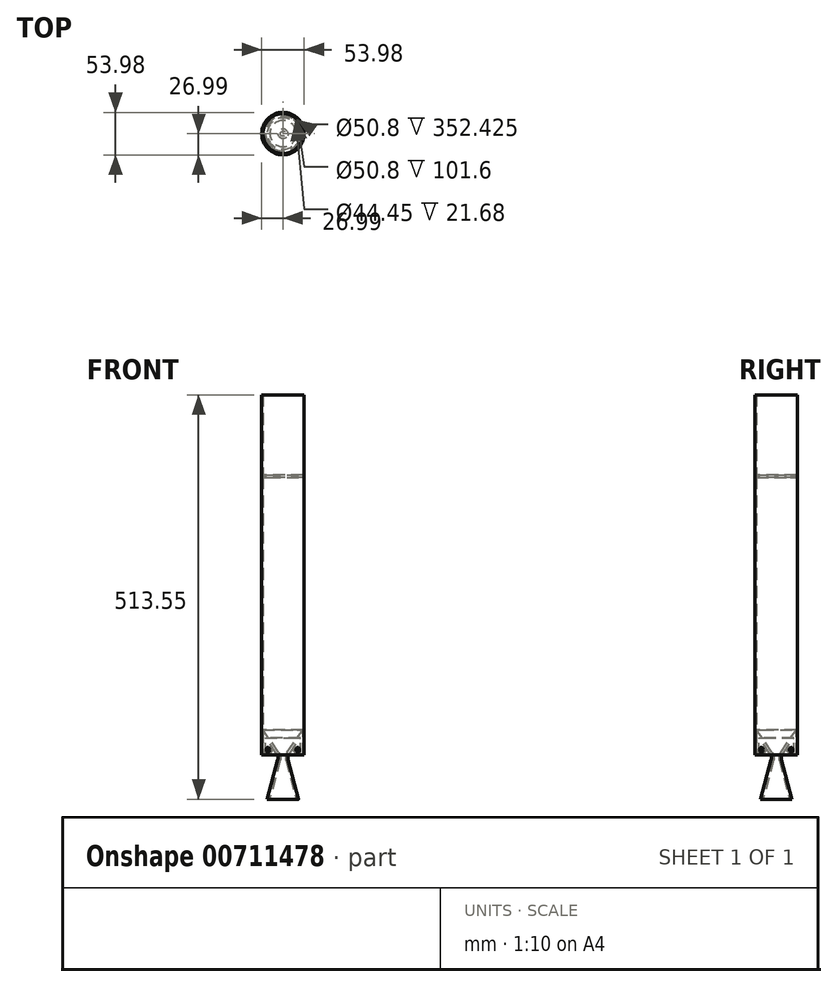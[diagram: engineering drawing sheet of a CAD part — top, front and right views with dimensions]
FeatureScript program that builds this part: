
annotation { "Feature Type Name" : "Feature", "Feature Type Description" : "" }
export const myFeature = defineFeature(function(context is Context, id is Id, definition is map)
    precondition{}
    {
        {
            var Q0;
            Q0=qCreatedBy(makeId("Front.planeOp"),FACE);
            var sketch = newSketch(context, id + "F0", { "sketchPlane" : qUnion([Q0])});
            skLineSegment(sketch, "E0", {"start": v(0, 0) * mm, "end": v(-25.4, 0) * mm, "construction": true});
            skLineSegment(sketch, "E1", {"start": v(-25.4, 0) * mm, "end": v(-5.47, -28.46) * mm});
            skArc(sketch, "E2", {"start": v(-5.47, -28.46) * mm, "mid": v(-3.37, -33.54) * mm, "end": v(-3.6, -39.03) * mm});
            skLineSegment(sketch, "E3", {"start": v(-3.18, -35.74) * mm, "end": v(0, -35.74) * mm, "construction": true});
            skLineSegment(sketch, "E4", {"start": v(-3.6, -39.03) * mm, "end": v(-16.76, -88.1) * mm});
            skLineSegment(sketch, "E5", {"start": v(-25.4, 0) * mm, "end": v(-25.4, -31.75) * mm});
            skLineSegment(sketch, "E6", {"start": v(-25.4, -31.75) * mm, "end": v(-22.22, -31.75) * mm});
            skLineSegment(sketch, "E7", {"start": v(-22.23, -10.07) * mm, "end": v(-8.07, -30.28) * mm});
            skLineSegment(sketch, "E8", {"start": v(-5.47, -28.46) * mm, "end": v(-8.07, -30.28) * mm, "construction": true});
            skLineSegment(sketch, "E9", {"start": v(-22.22, -31.75) * mm, "end": v(-22.22, -10.07) * mm});
            skLineSegment(sketch, "E10", {"start": v(-3.6, -39.03) * mm, "end": v(-6.67, -38.21) * mm, "construction": true});
            skArc(sketch, "E11", {"start": v(-6.67, -38.21) * mm, "mid": v(-6.5, -34.1) * mm, "end": v(-8.07, -30.28) * mm});
            skLineSegment(sketch, "E12", {"start": v(0, 0) * mm, "end": v(0, -88.1) * mm, "construction": true});
            skLineSegment(sketch, "E13", {"start": v(0, -88.1) * mm, "end": v(-16.76, -88.1) * mm, "construction": true});
            skLineSegment(sketch, "E14", {"start": v(-6.67, -38.21) * mm, "end": v(-20.04, -88.1) * mm});
            skLineSegment(sketch, "E15", {"start": v(-20.04, -88.1) * mm, "end": v(-16.76, -88.1) * mm});
            skSolve(sketch);
        }
        {
            var Q0;
            Q0=makeQuery(id+"F0.imprint","IMPRINT",FACE,{"disambiguationData":[TD([[makeQuery(id+"F0.imprint","IMPRINT",EDGE,{"derivedFrom":sQuery(id+"F0.wireOp",EDGE,"E1")}),-1.0]])]});
            var Q1;
            Q1=sQuery(id+"F0.wireOp",EDGE,"E12");
            revolve(context, id + "F1", {"surfaceOperationType" : NewSurfaceOperationType.NEW, "entities" : qUnion([Q0]), "axis" : qUnion([Q1]), "revolveType" : RevolveType.FULL});
        }
        {
            var Q0;
            Q0=qCreatedBy(makeId("Front.planeOp"),FACE);
            var sketch = newSketch(context, id + "F2", { "sketchPlane" : qUnion([Q0])});
            skLineSegment(sketch, "E16", {"start": v(0, 0) * mm, "end": v(0, 457.2) * mm, "construction": true});
            skLineSegment(sketch, "E17", {"start": v(0, 457.2) * mm, "end": v(25.4, 457.2) * mm, "construction": true});
            skLineSegment(sketch, "E18", {"start": v(25.4, 457.2) * mm, "end": v(26.99, 457.2) * mm});
            skLineSegment(sketch, "E19", {"start": v(26.99, 457.2) * mm, "end": v(26.99, 0) * mm});
            skLineSegment(sketch, "E20", {"start": v(26.99, 0) * mm, "end": v(25.4, 0) * mm});
            skLineSegment(sketch, "E21", {"start": v(25.4, 0) * mm, "end": v(25.4, 352.43) * mm});
            skLineSegment(sketch, "E22", {"start": v(-15.92, 457.2) * mm, "end": v(-15.92, 355.6) * mm, "construction": true});
            skLineSegment(sketch, "E23", {"start": v(-15.92, 355.6) * mm, "end": v(0, 355.6) * mm, "construction": true});
            skLineSegment(sketch, "E24", {"start": v(0, 355.6) * mm, "end": v(25.4, 355.6) * mm});
            skLineSegment(sketch, "E25", {"start": v(0, 355.6) * mm, "end": v(0, 352.43) * mm});
            skLineSegment(sketch, "E26", {"start": v(0, 352.43) * mm, "end": v(25.4, 352.43) * mm});
            skLineSegment(sketch, "E27.trimOffspring", {"start": v(25.4, 355.6) * mm, "end": v(25.4, 457.2) * mm});
            skSolve(sketch);
        }
        {
            var Q0;
            Q0=makeQuery(id+"F2.imprint","IMPRINT",FACE,{"disambiguationData":[TD([[makeQuery(id+"F2.imprint","IMPRINT",EDGE,{"derivedFrom":sQuery(id+"F2.wireOp",EDGE,"E18")}),-1.0]])]});
            var Q1;
            Q1=sQuery(id+"F2.wireOp",EDGE,"E16");
            revolve(context, id + "F3", {"operationType" : NewBodyOperationType.ADD, "surfaceOperationType" : NewSurfaceOperationType.NEW, "entities" : qUnion([Q0]), "axis" : qUnion([Q1]), "revolveType" : RevolveType.FULL});
        }
        {
            var Q0;
            Q0=makeQuery(id+"F1.opRevolve","SWEPT_BODY",BODY,{"disambiguationData":[OSD([sQuery(id+"F0.wireOp",EDGE,"E1"),sQuery(id+"F0.wireOp",EDGE,"E2"),sQuery(id+"F0.wireOp",EDGE,"E4"),sQuery(id+"F0.wireOp",EDGE,"E5"),sQuery(id+"F0.wireOp",EDGE,"E6"),sQuery(id+"F0.wireOp",EDGE,"E7"),sQuery(id+"F0.wireOp",EDGE,"E9"),sQuery(id+"F0.wireOp",EDGE,"E11"),sQuery(id+"F0.wireOp",EDGE,"iXrRLQ2d-38gj-TsyJ-HKGC-BAWMquZrdBay"),sQuery(id+"F0.wireOp",EDGE,"QxqG3yJh-0K9V-yYqa-KfpX-jcyM5mLZCGYJ")])]});
            transform(context, id + "F4", {"entities" : qUnion([Q0]), "transformType" : TransformType.TRANSLATION_3D, "dx" : 0 * mm, "dy" : 0 * mm, "dz" : 31.75 * mm, "makeCopy" : false});
        }
        {
            var Q0;
            Q0=qCreatedBy(makeId("Right.planeOp"),FACE);
            cPlane(context, id + "F5", {"entities" : qUnion([Q0]), "cplaneType" : CPlaneType.OFFSET, "offset" : 20.32 * mm, "width" : 152.4 * mm, "height" : 152.4 * mm});
        }
        {
            var Q0;
            Q0=qCreatedBy(id+"F5.planeOp",FACE);
            var sketch = newSketch(context, id + "F6", { "sketchPlane" : qUnion([Q0])});
            skLineSegment(sketch, "E28", {"start": v(0, 0) * mm, "end": v(0, 6.35) * mm, "construction": true});
            skCircle(sketch, "E29", {"center": v(0, 6.35) * mm, "radius": 3.18 * mm});
            skSolve(sketch);
        }
        {
            var Q0;
            Q0 = qSketchRegion(id + "F6", true);
            extrude(context, id + "F7", {"entities" : qUnion([Q0]), "operationType" : NewBodyOperationType.REMOVE, "depth" : 25.4 * mm, "offsetDistance" : 25.4 * mm});
        }
        {
            var Q0;
            Q0=qCreatedBy(makeId("Right.planeOp"),FACE);
            cPlane(context, id + "F8", {"entities" : qUnion([Q0]), "cplaneType" : CPlaneType.OFFSET, "offset" : 20.32 * mm, "oppositeDirection" : true, "width" : 152.4 * mm, "height" : 152.4 * mm});
        }
        {
            var Q0;
            Q0=qCreatedBy(id+"F8.planeOp",FACE);
            var sketch = newSketch(context, id + "F9", { "sketchPlane" : qUnion([Q0])});
            skLineSegment(sketch, "E30", {"start": v(0, 0) * mm, "end": v(0, 6.35) * mm, "construction": true});
            skCircle(sketch, "E31", {"center": v(0, 6.35) * mm, "radius": 3.18 * mm});
            skSolve(sketch);
        }
        {
            var Q0;
            Q0 = qSketchRegion(id + "F9", true);
            extrude(context, id + "F10", {"entities" : qUnion([Q0]), "operationType" : NewBodyOperationType.REMOVE, "oppositeDirection" : true, "depth" : 25.4 * mm, "offsetDistance" : 25.4 * mm});
        }
        {
            var Q0;
            Q0 = qSketchRegion(id + "F6", true);
            extrude(context, id + "F11", {"entities" : qUnion([Q0]), "operationType" : NewBodyOperationType.REMOVE, "depth" : 25.4 * mm, "offsetDistance" : 25.4 * mm});
        }
        {
            var Q0;
            Q0=qCreatedBy(makeId("Front.planeOp"),FACE);
            cPlane(context, id + "F12", {"entities" : qUnion([Q0]), "cplaneType" : CPlaneType.OFFSET, "offset" : 20.32 * mm, "width" : 152.4 * mm, "height" : 152.4 * mm});
        }
        {
            var Q0;
            Q0=qCreatedBy(id+"F12.planeOp",FACE);
            var sketch = newSketch(context, id + "F13", { "sketchPlane" : qUnion([Q0])});
            skLineSegment(sketch, "E32", {"start": v(0, 0) * mm, "end": v(0, 6.35) * mm, "construction": true});
            skCircle(sketch, "E33", {"center": v(0, 6.35) * mm, "radius": 3.18 * mm});
            skSolve(sketch);
        }
        {
            var Q0;
            Q0 = qSketchRegion(id + "F13", true);
            extrude(context, id + "F14", {"entities" : qUnion([Q0]), "operationType" : NewBodyOperationType.REMOVE, "depth" : 25.4 * mm, "offsetDistance" : 25.4 * mm});
        }
        {
            var Q0;
            Q0=qCreatedBy(makeId("Front.planeOp"),FACE);
            cPlane(context, id + "F15", {"entities" : qUnion([Q0]), "cplaneType" : CPlaneType.OFFSET, "offset" : 20.32 * mm, "oppositeDirection" : true, "width" : 152.4 * mm, "height" : 152.4 * mm});
        }
        {
            var Q0;
            Q0=qCreatedBy(id+"F15.planeOp",FACE);
            var sketch = newSketch(context, id + "F16", { "sketchPlane" : qUnion([Q0])});
            skLineSegment(sketch, "E34", {"start": v(0, 0) * mm, "end": v(0, 6.35) * mm, "construction": true});
            skCircle(sketch, "E35", {"center": v(0, 6.35) * mm, "radius": 3.18 * mm});
            skSolve(sketch);
        }
        {
            var Q0;
            Q0 = qSketchRegion(id + "F16", true);
            extrude(context, id + "F17", {"entities" : qUnion([Q0]), "operationType" : NewBodyOperationType.REMOVE, "oppositeDirection" : true, "depth" : 25.4 * mm, "offsetDistance" : 25.4 * mm});
        }
        {
            var Q0;
            Q0=makeQuery(id+"F1.opRevolve","SWEPT_BODY",BODY,{"disambiguationData":[OSD([sQuery(id+"F0.wireOp",EDGE,"E1"),sQuery(id+"F0.wireOp",EDGE,"E2"),sQuery(id+"F0.wireOp",EDGE,"E4"),sQuery(id+"F0.wireOp",EDGE,"E5"),sQuery(id+"F0.wireOp",EDGE,"E6"),sQuery(id+"F0.wireOp",EDGE,"E7"),sQuery(id+"F0.wireOp",EDGE,"E9"),sQuery(id+"F0.wireOp",EDGE,"E11"),sQuery(id+"F0.wireOp",EDGE,"iXrRLQ2d-38gj-TsyJ-HKGC-BAWMquZrdBay"),sQuery(id+"F0.wireOp",EDGE,"QxqG3yJh-0K9V-yYqa-KfpX-jcyM5mLZCGYJ")])]});
            var Q1;
            Q1=makeQuery(id+"F3.opRevolve","SWEPT_BODY",BODY,{"disambiguationData":[OSD([sQuery(id+"F2.wireOp",EDGE,"E18"),sQuery(id+"F2.wireOp",EDGE,"E19"),sQuery(id+"F2.wireOp",EDGE,"E20"),sQuery(id+"F2.wireOp",EDGE,"E21"),sQuery(id+"F2.wireOp",EDGE,"E24"),sQuery(id+"F2.wireOp",EDGE,"E25"),sQuery(id+"F2.wireOp",EDGE,"E26"),sQuery(id+"F2.wireOp",EDGE,"E27.trimOffspring")])]});
            var Q2;
            Q2=makeQuery(id+"F3.opRevolve","SWEPT_EDGE",EDGE,{"disambiguationData":[OSD([sQuery(id+"F2.wireOp",EDGE,"E18"),sQuery(id+"F2.wireOp",EDGE,"E19")])]});
            transform(context, id + "F18", {"entities" : qUnion([Q0, Q1]), "transformType" : TransformType.ROTATION, "transformAxis" : qUnion([Q2]), "angle" : 45 * degree, "makeCopy" : false});
        }
    });
